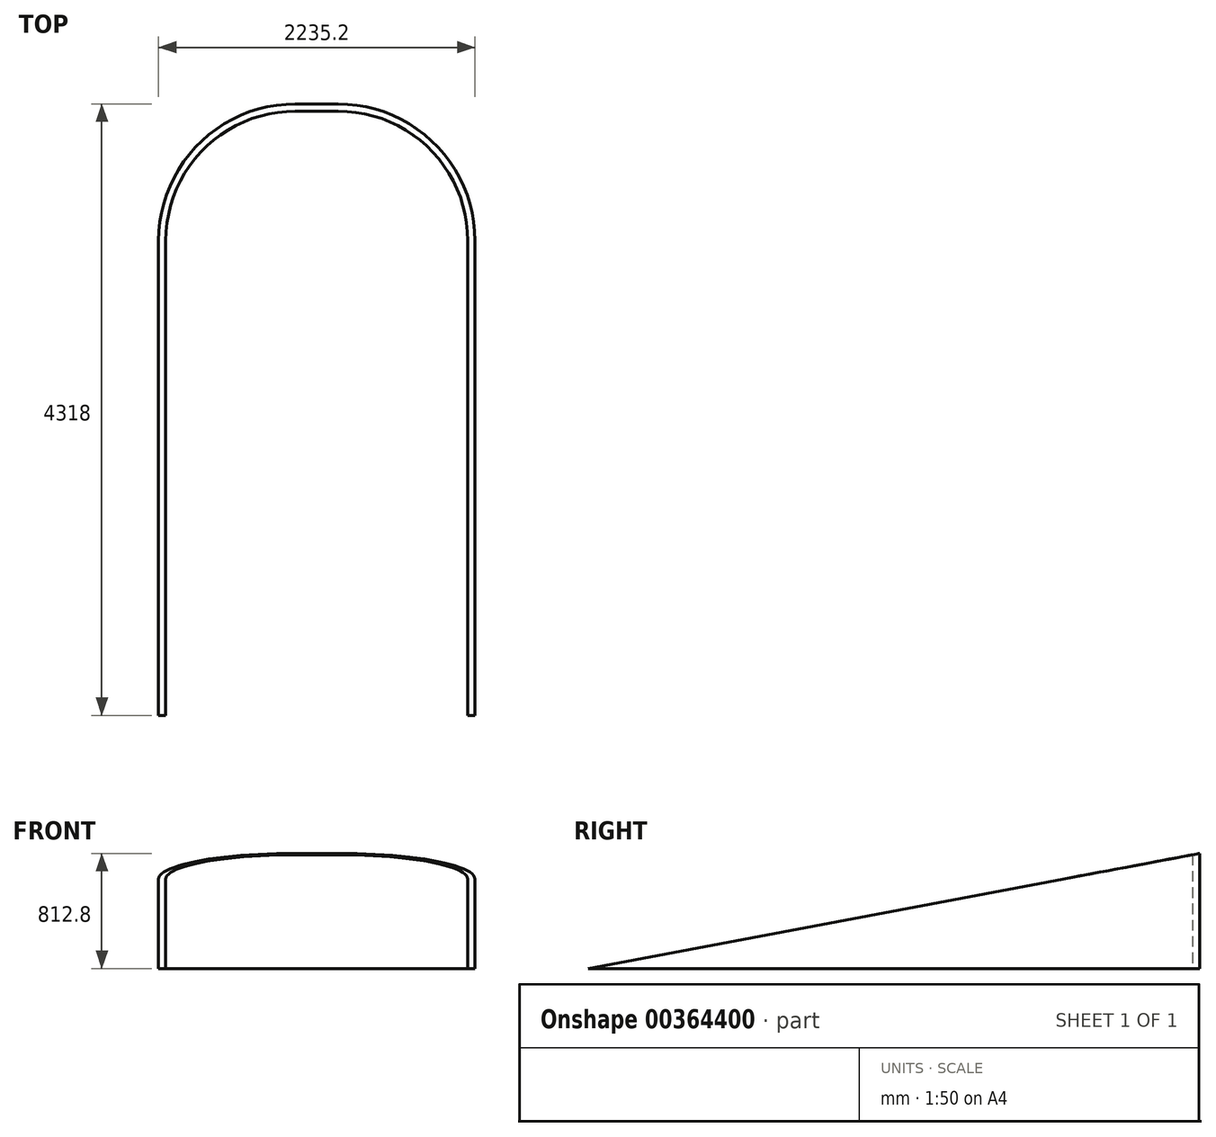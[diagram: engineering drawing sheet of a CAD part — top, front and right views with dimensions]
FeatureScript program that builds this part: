
annotation { "Feature Type Name" : "Feature", "Feature Type Description" : "" }
export const myFeature = defineFeature(function(context is Context, id is Id, definition is map)
    precondition{}
    {
        {
            var Q0;
            Q0=qCreatedBy(makeId("Top.planeOp"),FACE);
            var sketch = newSketch(context, id + "F0", { "sketchPlane" : qUnion([Q0])});
            skLineSegment(sketch, "E0.bottom", {"start": v(-107.95, 2133.6) * mm, "end": v(196.85, 2133.6) * mm});
            skLineSegment(sketch, "E0.left", {"start": v(-1022.35, 1219.2) * mm, "end": v(-1022.35, -2133.6) * mm});
            skLineSegment(sketch, "E0.right", {"start": v(1111.25, 1219.2) * mm, "end": v(1111.25, -2133.6) * mm});
            skArc(sketch, "E1.filletArc", {"start": v(-107.95, 2133.6) * mm, "mid": v(-754.53, 1865.78) * mm, "end": v(-1022.35, 1219.2) * mm});
            skArc(sketch, "E2.filletArc", {"start": v(1111.25, 1219.2) * mm, "mid": v(843.43, 1865.78) * mm, "end": v(196.85, 2133.6) * mm});
            skLineSegment(sketch, "E3.0", {"start": v(-1073.15, 1219.2) * mm, "end": v(-1073.15, -2133.6) * mm});
            skLineSegment(sketch, "E3.1", {"start": v(1162.05, 1219.2) * mm, "end": v(1162.05, -2133.6) * mm});
            skArc(sketch, "E3.2", {"start": v(1162.05, 1219.2) * mm, "mid": v(879.35, 1901.7) * mm, "end": v(196.85, 2184.4) * mm});
            skLineSegment(sketch, "E3.3", {"start": v(-107.95, 2184.4) * mm, "end": v(196.85, 2184.4) * mm});
            skArc(sketch, "E3.4", {"start": v(-107.95, 2184.4) * mm, "mid": v(-790.45, 1901.7) * mm, "end": v(-1073.15, 1219.2) * mm});
            skLineSegment(sketch, "E4", {"start": v(-1073.15, -2133.6) * mm, "end": v(-1022.35, -2133.6) * mm});
            skLineSegment(sketch, "E5", {"start": v(1111.25, -2133.6) * mm, "end": v(1162.05, -2133.6) * mm});
            skSolve(sketch);
        }
        {
            var Q0;
            Q0 = qSketchRegion(id + "F0", true);
            extrude(context, id + "F1", {"entities" : qUnion([Q0]), "depth" : 1219.2 * mm});
        }
        {
            var Q0;
            Q0=makeQuery(id+"F1.opExtrude","SWEPT_FACE",FACE,{"disambiguationData":[OSD([sQuery(id+"F0.wireOp",EDGE,"E3.1")])]});
            var sketch = newSketch(context, id + "F2", { "sketchPlane" : qUnion([Q0])});
            skLineSegment(sketch, "E6", {"start": v(2184.4, 1219.2) * mm, "end": v(-2133.6, 1219.2) * mm});
            skLineSegment(sketch, "E7", {"start": v(-2133.6, 1219.2) * mm, "end": v(-2133.6, 609.6) * mm});
            skLineSegment(sketch, "E8", {"start": v(2184.4, 1219.2) * mm, "end": v(2184.4, 812.8) * mm});
            skLineSegment(sketch, "E9", {"start": v(2184.4, 812.8) * mm, "end": v(-2133.6, 0) * mm});
            skLineSegment(sketch, "E10", {"start": v(-2133.6, 0) * mm, "end": v(-2133.6, 609.6) * mm});
            skSolve(sketch);
        }
        {
            var Q0;
            Q0 = qSketchRegion(id + "F2", true);
            extrude(context, id + "F3", {"entities" : qUnion([Q0]), "operationType" : NewBodyOperationType.REMOVE, "endBound" : BoundingType.THROUGH_ALL, "oppositeDirection" : true, "depth" : 25.4 * mm});
        }
    });
